# Revit family: CADS_Vent-Axia_MechEquip_Fan_ESP_1Ph6P - SUPPLY
name_source: partatom
category: Mechanical Equipment
units: mm (PartAtom-declared; Revit-internal decimal feet)

## family parameters
Always vertical = Yes
Cut with Voids When Loaded = No
OmniClass Number = 23.75.00.00
OmniClass Title = Climate Control (HVAC)
Part Type = Normal
Room Calculation Point = No
Round Connector Dimension = Use Diameter
Shared = No
Work Plane-Based = No

## types (5) — shared parameters
AirflowRateRange = 0.0 L/s
AssemblyPlace = UNKNOWN
AssetType = FIXED
DurationUnit = Year
ExteriorInsulation = No
Fitting Type = Ignore
GrossWeight = 0.00 kg
HasProtectiveEarth = No
IfcExportAs = IfcFanType
IsExtendedWarranty = No
ManufacturerAddress = Fleming Way
Crawley 
RH10 9YX
Quantity = 1
RatedCurrent = 0 A
RatedVoltage = 0 V
Status = New
WarrantyGuarantor = Vent-Axia Limited
WorkingPressure = 0.0 Pa
zero-valued in all types: CADS_Index, CADS_Usage, Default Elevation, ExpectedServiceLife, NumberOfPoles

## per-type parameters (varying)
| type | A | E | G | ModelReference | NominalDiameter | NominalHeight | NominalLength | NominalWidth | nd |
| T100_ESP35516 | 485 mm  [stored 1.59121 ft] | 86 mm  [stored 0.282152 ft] | 21 mm  [stored 0.0688976 ft] | AXIAL PLATE FAN 355DIA 1PH 6 POLE | 355 mm | 485 mm  [stored 1.59121 ft] | 97 mm  [stored 0.318241 ft] | 485 mm  [stored 1.59121 ft] | 355 mm |
| T100_ESP40016 | 540 mm  [stored 1.77165 ft] | 93 mm  [stored 0.305118 ft] | 12 mm  [stored 0.0393701 ft] | AXIAL PLATE FAN 400DIA 1PH 6 POLE | 400 mm  [stored 1.31234 ft] | 540 mm  [stored 1.77165 ft] | 100 mm  [stored 0.328084 ft] | 540 mm  [stored 1.77165 ft] | 400 mm  [stored 1.31234 ft] |
| T100_ESP40016B | 540 mm  [stored 1.77165 ft] | 93 mm  [stored 0.305118 ft] | 12 mm  [stored 0.0393701 ft] | 400MM 1PH 6P PLATE FAN FC040-6EQ.2F.A7 163383 | 400 mm  [stored 1.31234 ft] | 540 mm  [stored 1.77165 ft] | 100 mm  [stored 0.328084 ft] | 540 mm  [stored 1.77165 ft] | 400 mm  [stored 1.31234 ft] |
| T100_ESP63016B | 805 mm  [stored 2.64108 ft] | 82 mm  [stored 0.269029 ft] | 20 mm  [stored 0.0656168 ft] | 630MM 1PH 6P PLATE FAN FC063-6EQ.4I.A7 169502 | 630 mm  [stored 2.06693 ft] | 805 mm  [stored 2.64108 ft] | 139 mm  [stored 0.456037 ft] | 805 mm  [stored 2.64108 ft] | 630 mm  [stored 2.06693 ft] |
| T100_ESP71016 | 850 mm  [stored 2.78871 ft] | 37 mm  [stored 0.121391 ft] | 20 mm  [stored 0.0656168 ft] | AXIAL PLATE FAN 710DIA 1PH 6 POLE | 710 mm  [stored 2.3294 ft] | 850 mm  [stored 2.78871 ft] | 141 mm | 850 mm  [stored 2.78871 ft] | 710 mm  [stored 2.3294 ft] |

note: column(s) folded — value = type name in every type: ModelNumber

note: [stored X ft] marks values corroborated as IEEE doubles in the binary element streams (Revit-internal decimal feet)

## geometry (parser evidence)
native form markers: Sweep x13
no freeform markers — native parametric forms only
